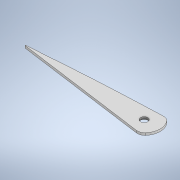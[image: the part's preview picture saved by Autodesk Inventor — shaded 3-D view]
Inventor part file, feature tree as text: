
AUTODESK INVENTOR PART (.ipt)
format: ipt  version: 2022 (Build 260153000, 153)  size: 147,456 bytes
history: native  units: mm
features: extrude x1, sketch x1
ambient origin geometry x8: Origin, YZ Plane, XZ Plane, XY Plane, X Axis, Y Axis, Z Axis, Center Point
bodies: Body1 (feature_tree)
feature tree (2):
  extrude  "Extrusion4"  Depth=8.0mm
  sketch  "Sketch1"  dims[d5=160.0mm d25=6.0mm d26=5.0mm d27=5.0mm d31=34.456mm d41=23.0mm d60=8.0mm d63=2.5mm d64=0.0mm d65=8.0mm]
